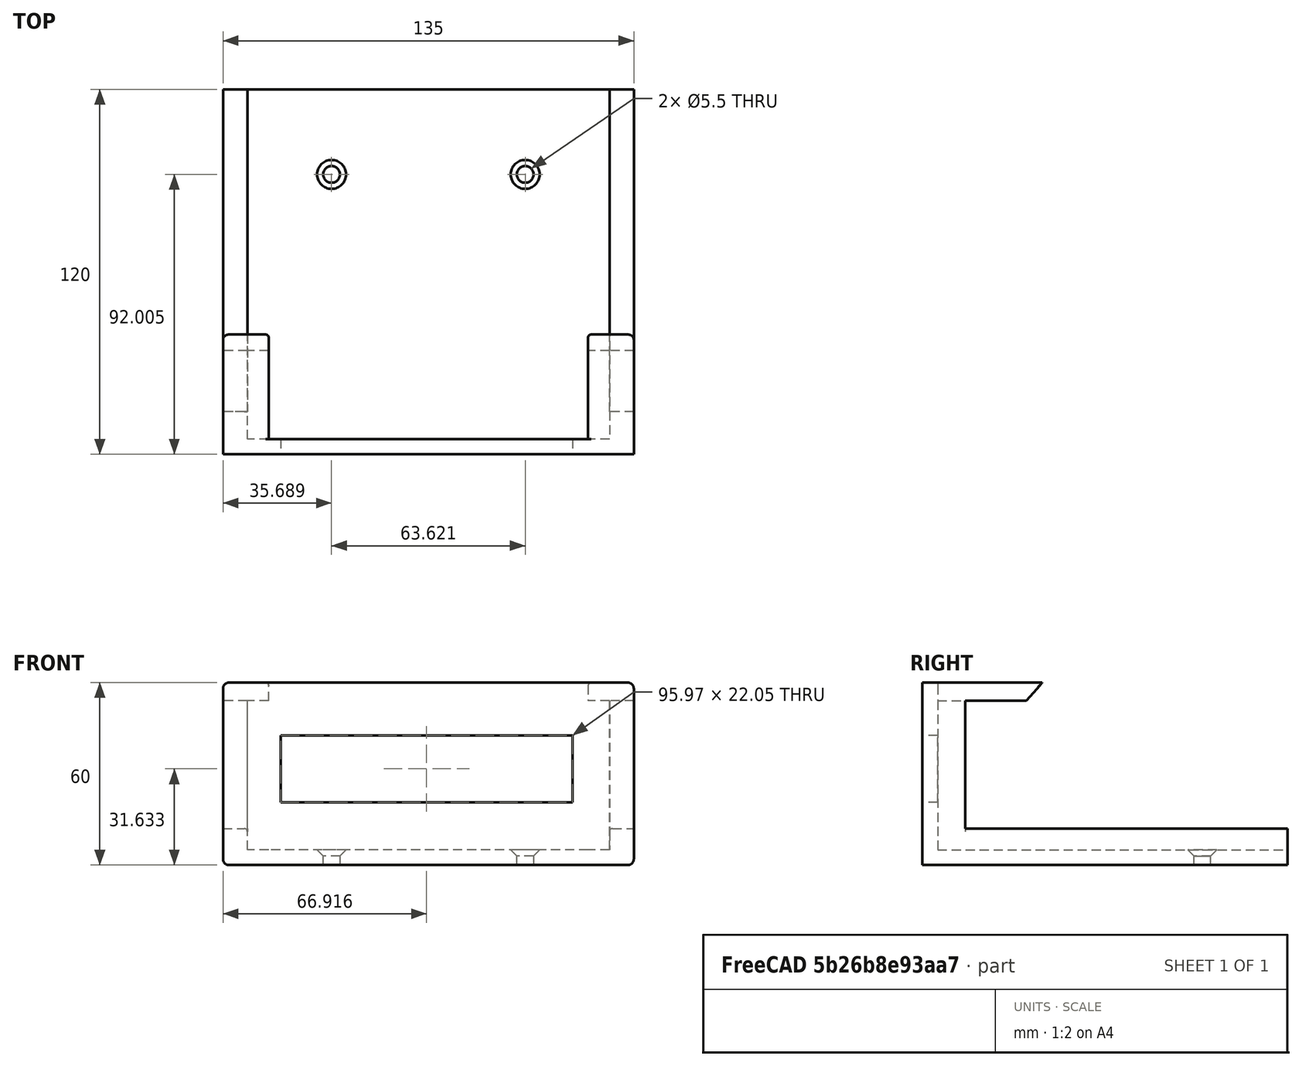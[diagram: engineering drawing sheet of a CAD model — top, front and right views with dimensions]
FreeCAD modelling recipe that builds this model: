
FCSTD DOCUMENT  (FreeCAD 0.19R)
Label: NucMount
License: All rights reserved
LicenseURL: http://en.wikipedia.org/wiki/All_rights_reserved
objects: Sketcher::SketchObject×6, PartDesign::Pocket×5, PartDesign::Fillet×3, PartDesign::Pad×1, PartDesign::Chamfer×1, PartDesign::Body×1, Mesh::Feature×1
note: 27 computed .brp shape members not serialized (recipe doc carries the construction recipe); baked Part::Feature solids carry a one-line shape summary decoded from their .brp

FEATURE [Sketcher::SketchObject] Sketch
  FullyConstrained = true
  MapMode = 5
  Support = -> [XY_Plane]
  sketch-geometry (4):
    g0: LineSegment StartX=-67.5 StartY=90 StartZ=0 EndX=67.5 EndY=90 EndZ=0
    g1: LineSegment StartX=67.5 StartY=90 StartZ=0 EndX=67.5 EndY=-30 EndZ=0
    g2: LineSegment StartX=67.5 StartY=-30 StartZ=0 EndX=-67.5 EndY=-30 EndZ=0
    g3: LineSegment StartX=-67.5 StartY=-30 StartZ=0 EndX=-67.5 EndY=90 EndZ=0
  constraints (11):
    c: Coincident(g0,g1)
    c: Coincident(g1,g2)
    c: Coincident(g2,g3)
    c: Coincident(g3,g0)
    c: Horizontal(g2)
    c: Vertical(g1)
    c: Vertical(g3)
    c: Distance(g0) = 135
    c: DistanceY(g1) = -30
    c: Symmetric(g0,g0,g-2)
    c: Distance(g1) = 120
FEATURE [PartDesign::Pad] Pad
  Direction = (1,1,1)
  Length = 60
  Length2 = 100
  Profile = -> Sketch
  Type = 0
FEATURE [Sketcher::SketchObject] Sketch001
  FullyConstrained = false
  MapMode = 5
  Placement = pos=(0,0,60) rot=(0,0,1;0rad)
  Support = -> [Pad]
  sketch-geometry (4):
    g0: LineSegment StartX=-52.5 StartY=119.365 StartZ=0 EndX=52.5 EndY=119.365 EndZ=0
    g1: LineSegment StartX=52.5 StartY=119.365 StartZ=0 EndX=52.5 EndY=-25 EndZ=0
    g2: LineSegment StartX=52.5 StartY=-25 StartZ=0 EndX=-52.5 EndY=-25 EndZ=0
    g3: LineSegment StartX=-52.5 StartY=-25 StartZ=0 EndX=-52.5 EndY=119.365 EndZ=0
  constraints (10):
    c: Coincident(g0,g1)
    c: Coincident(g1,g2)
    c: Coincident(g2,g3)
    c: Coincident(g3,g0)
    c: Horizontal(g0)
    c: Vertical(g1)
    c: Vertical(g3)
    c: Symmetric(g1,g2,g-2)
    c: DistanceY(g1) = -25
    c: Distance(g2) = 105
FEATURE [PartDesign::Pocket] Pocket
  BaseFeature = -> Pad
  Length = 55
  Length2 = 100
  Profile = -> Sketch001
  Type = 0
FEATURE [Sketcher::SketchObject] Sketch005
  FullyConstrained = false
  MapMode = 5
  Placement = pos=(0,-25,0) rot=(0,0.707107,0.707107;3.14159rad)
  Support = -> [Pocket]
  sketch-geometry (4):
    g0: LineSegment StartX=-47.401 StartY=42.6571 StartZ=0 EndX=48.5692 EndY=42.6571 EndZ=0
    g1: LineSegment StartX=48.5692 StartY=42.6571 StartZ=0 EndX=48.5692 EndY=20.6086 EndZ=0
    g2: LineSegment StartX=48.5692 StartY=20.6086 StartZ=0 EndX=-47.401 EndY=20.6086 EndZ=0
    g3: LineSegment StartX=-47.401 StartY=20.6086 StartZ=0 EndX=-47.401 EndY=42.6571 EndZ=0
  constraints (8):
    c: Coincident(g0,g1)
    c: Coincident(g1,g2)
    c: Coincident(g2,g3)
    c: Coincident(g3,g0)
    c: Horizontal(g0)
    c: Horizontal(g2)
    c: Vertical(g1)
    c: Vertical(g3)
FEATURE [PartDesign::Pocket] Pocket001
  BaseFeature = -> Pocket
  Length = 5
  Length2 = 100
  Profile = -> Sketch005
  Type = 1
FEATURE [Sketcher::SketchObject] Sketch004
  FullyConstrained = false
  MapMode = 5
  Placement = pos=(67.5,0,0) rot=(0.57735,0.57735,0.57735;2.0944rad)
  Support = -> [Pocket001]
  sketch-geometry (6):
    g0: LineSegment StartX=-15.9331 StartY=54 StartZ=0 EndX=4.13603 EndY=54 EndZ=0
    g1: LineSegment StartX=201.891 StartY=12 StartZ=0 EndX=-15.9331 EndY=12 EndZ=0
    g2: LineSegment StartX=-15.9331 StartY=12 StartZ=0 EndX=-15.9331 EndY=54 EndZ=0
    g3: LineSegment StartX=4.13603 StartY=54 StartZ=0 EndX=16.8226 EndY=68.4884 EndZ=0
    g4: LineSegment StartX=16.8226 StartY=68.4884 StartZ=0 EndX=154.675 EndY=67.0614 EndZ=0
    g5: LineSegment StartX=154.675 StartY=67.0614 StartZ=0 EndX=201.891 EndY=12 EndZ=0
  constraints (11):
    c: Coincident(g1,g2)
    c: Coincident(g2,g0)
    c: Horizontal(g0)
    c: Vertical(g2)
    c: DistanceY(g1) = 12
    c: DistanceY(g0) = 54
    c: Horizontal(g1)
    c: Coincident(g0,g3)
    c: Coincident(g3,g4)
    c: Coincident(g4,g5)
    c: Coincident(g5,g1)
FEATURE [PartDesign::Pocket] Pocket002
  BaseFeature = -> Pocket001
  Length = 5
  Length2 = 100
  Profile = -> Sketch004
  Type = 1
FEATURE [Sketcher::SketchObject] Sketch002
  FullyConstrained = false
  MapMode = 5
  Placement = pos=(0,0,5) rot=(0,0,1;0rad)
  Support = -> [Pocket002]
  sketch-geometry (4):
    g0: LineSegment StartX=-59.5 StartY=105.882 StartZ=0 EndX=59.5 EndY=105.882 EndZ=0
    g1: LineSegment StartX=59.5 StartY=105.882 StartZ=0 EndX=59.5 EndY=-25 EndZ=0
    g2: LineSegment StartX=59.5 StartY=-25 StartZ=0 EndX=-59.5 EndY=-25 EndZ=0
    g3: LineSegment StartX=-59.5 StartY=-25 StartZ=0 EndX=-59.5 EndY=105.882 EndZ=0
  constraints (10):
    c: Coincident(g0,g1)
    c: Coincident(g1,g2)
    c: Coincident(g2,g3)
    c: Coincident(g3,g0)
    c: Horizontal(g0)
    c: Vertical(g1)
    c: Vertical(g3)
    c: Distance(g0) = 119
    c: Symmetric(g1,g2,g-2)
    c: DistanceY(g1) = -25
FEATURE [PartDesign::Pocket] Pocket003
  BaseFeature = -> Pocket002
  Length = 49
  Length2 = 100
  Profile = -> Sketch002
  Reversed = true
  Type = 0
FEATURE [Sketcher::SketchObject] Sketch006
  FullyConstrained = false
  MapMode = 5
  Placement = pos=(0,0,5) rot=(0,0,1;0rad)
  Support = -> [Pocket003]
  sketch-geometry (2):
    g0: Circle CenterX=-31.8105 CenterY=62.0049 CenterZ=0 NormalX=0 NormalY=0 NormalZ=1 AngleXU=0 Radius=2.75
    g1: Circle CenterX=31.8105 CenterY=62.0049 CenterZ=0 NormalX=0 NormalY=0 NormalZ=1 AngleXU=0 Radius=2.75
  constraints (3):
    c: Diameter(g0) = 5.5
    c: Equal(g0,g1)
    c: Symmetric(g1,g0,g-2)
FEATURE [PartDesign::Pocket] Pocket004
  BaseFeature = -> Pocket003
  Length = 5
  Length2 = 100
  Profile = -> Sketch006
  Type = 1
FEATURE [PartDesign::Chamfer] Chamfer
  Angle = 45
  Base = -> Pocket004 [Edge32,Edge33]
  BaseFeature = -> Pocket004
  ChamferType = 0
  FlipDirection = false
  Size = 2
  Size2 = 1
  SupportTransform = false
FEATURE [PartDesign::Fillet] Fillet
  Base = -> Chamfer [Edge56,Edge52,Edge70,Edge51]
  BaseFeature = -> Chamfer
  Radius = 2
  SupportTransform = false
FEATURE [PartDesign::Fillet] Fillet001
  Base = -> Fillet [Edge34,Edge37]
  BaseFeature = -> Fillet
  Radius = 1
  SupportTransform = false
FEATURE [PartDesign::Fillet] Fillet002
  Base = -> Fillet001 [Edge104,Edge103]
  BaseFeature = -> Fillet001
  Radius = 1
  SupportTransform = false
FEATURE [PartDesign::Body] Body
  Group = -> [Sketch,Pad,Sketch001,Pocket,Sketch002,Sketch004,Sketch005,Pocket001,Pocket002,Pocket003,Sketch006,Pocket004,Chamfer,Fillet,Fillet001,Fillet002]
  Origin = -> Origin
  Tip = -> Fillet002
FEATURE [Mesh::Feature] Mesh  label="Fillet002 (Meshed)"
